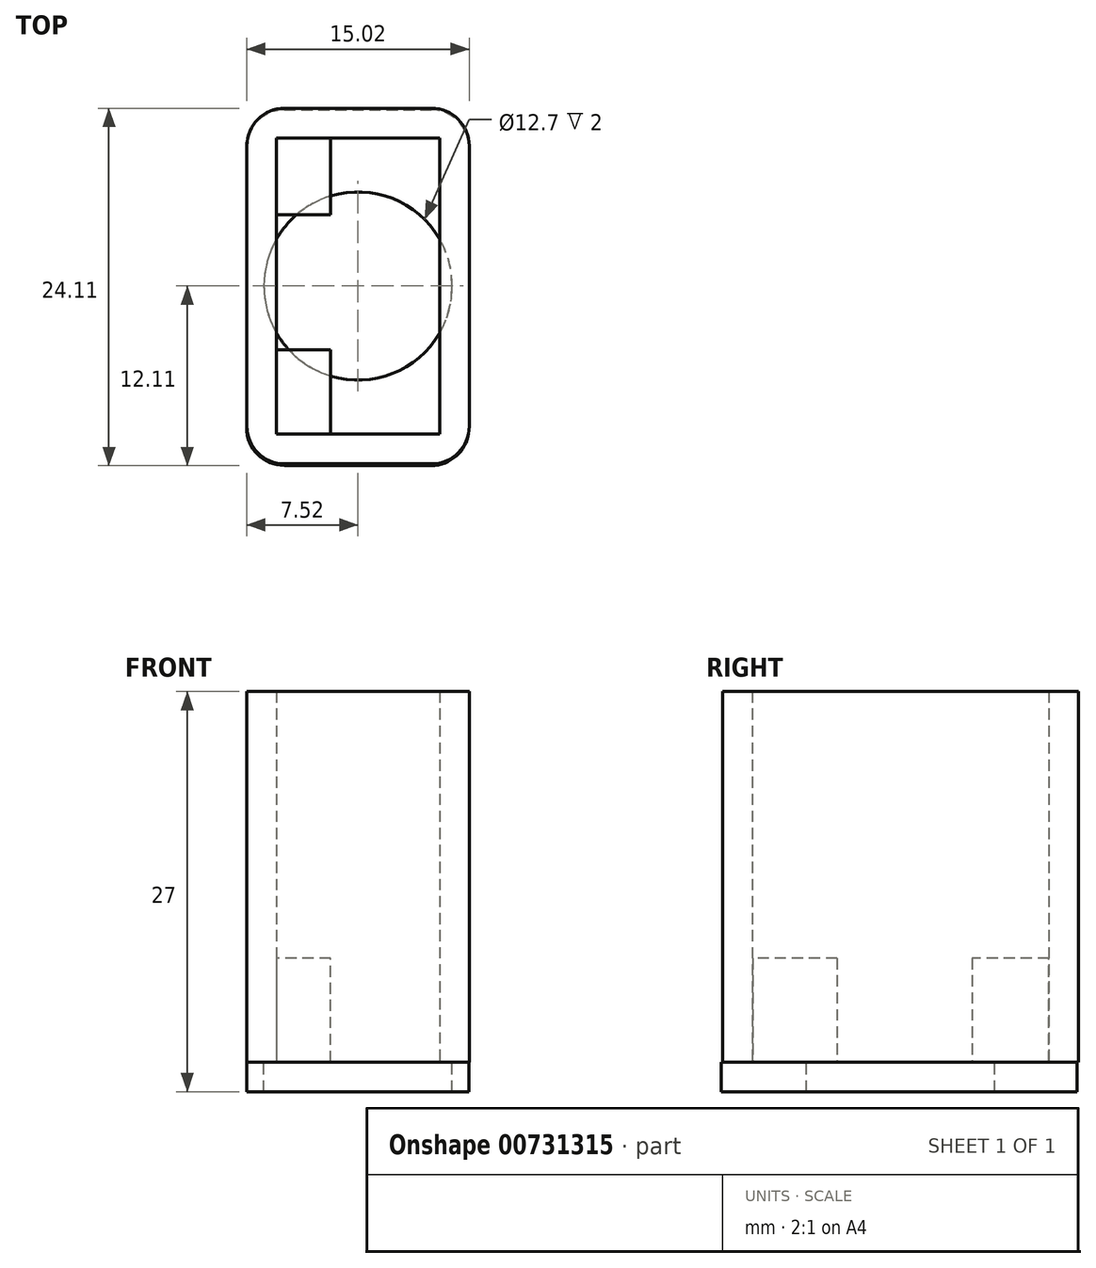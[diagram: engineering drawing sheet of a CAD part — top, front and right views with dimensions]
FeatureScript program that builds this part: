
annotation { "Feature Type Name" : "Feature", "Feature Type Description" : "" }
export const myFeature = defineFeature(function(context is Context, id is Id, definition is map)
    precondition{}
    {
        {
            var Q0;
            Q0=qCreatedBy(makeId("Top.planeOp"),FACE);
            var sketch = newSketch(context, id + "F0", { "sketchPlane" : qUnion([Q0])});
            skLineSegment(sketch, "E0.bottom", {"start": v(5.5, 10) * mm, "end": v(-5.5, 10) * mm});
            skLineSegment(sketch, "E0.top", {"start": v(5.5, -10) * mm, "end": v(-5.5, -10) * mm});
            skLineSegment(sketch, "E0.left", {"start": v(5.5, 10) * mm, "end": v(5.5, -10) * mm});
            skLineSegment(sketch, "E0.right", {"start": v(-5.5, 10) * mm, "end": v(-5.5, -10) * mm});
            skPoint(sketch, "E0.middle", {"position": v(0, 0) * mm});
            skLineSegment(sketch, "E1.bottom", {"start": v(4.96, 12) * mm, "end": v(-4.96, 12) * mm});
            skLineSegment(sketch, "E1.top", {"start": v(4.96, -12) * mm, "end": v(-4.96, -12) * mm});
            skLineSegment(sketch, "E1.left", {"start": v(7.5, 9.46) * mm, "end": v(7.5, -9.46) * mm});
            skLineSegment(sketch, "E1.right", {"start": v(-7.5, 9.46) * mm, "end": v(-7.5, -9.46) * mm});
            skPoint(sketch, "E2.visualSharp", {"position": v(-7.5, -12) * mm});
            skArc(sketch, "E2.filletArc", {"start": v(-7.5, -9.46) * mm, "mid": v(-6.76, -11.26) * mm, "end": v(-4.96, -12) * mm});
            skPoint(sketch, "E3.visualSharp", {"position": v(7.5, -12) * mm});
            skArc(sketch, "E3.filletArc", {"start": v(4.96, -12) * mm, "mid": v(6.76, -11.26) * mm, "end": v(7.5, -9.46) * mm});
            skPoint(sketch, "E4.visualSharp", {"position": v(7.5, 12) * mm});
            skArc(sketch, "E4.filletArc", {"start": v(7.5, 9.46) * mm, "mid": v(6.76, 11.26) * mm, "end": v(4.96, 12) * mm});
            skPoint(sketch, "E5.visualSharp", {"position": v(-7.5, 12) * mm});
            skArc(sketch, "E5.filletArc", {"start": v(-4.96, 12) * mm, "mid": v(-6.76, 11.26) * mm, "end": v(-7.5, 9.46) * mm});
            skSolve(sketch);
        }
        {
            var Q0;
            Q0=makeQuery(id+"F0.imprint","IMPRINT",FACE,{"disambiguationData":[TD([[makeQuery(id+"F0.imprint","IMPRINT",EDGE,{"derivedFrom":sQuery(id+"F0.wireOp",EDGE,"E0.bottom")}),-1.0]])]});
            extrude(context, id + "F1", {"entities" : qUnion([Q0]), "depth" : 25 * mm, "offsetDistance" : 25.4 * mm});
        }
        {
            var Q0;
            Q0=qCreatedBy(makeId("Top.planeOp"),FACE);
            var sketch = newSketch(context, id + "F2", { "sketchPlane" : qUnion([Q0])});
            skCircle(sketch, "E6", {"center": v(0, 0) * mm, "radius": 6.35 * mm});
            skLineSegment(sketch, "E7.bottom", {"start": v(-4.98, -12.1) * mm, "end": v(4.94, -12.1) * mm});
            skLineSegment(sketch, "E7.top", {"start": v(-4.98, 11.9) * mm, "end": v(4.94, 11.9) * mm});
            skLineSegment(sketch, "E7.left", {"start": v(-7.52, -9.57) * mm, "end": v(-7.52, 9.35) * mm});
            skLineSegment(sketch, "E7.right", {"start": v(7.48, -9.57) * mm, "end": v(7.48, 9.35) * mm});
            skPoint(sketch, "E8.visualSharp", {"position": v(-7.52, -12.1) * mm});
            skArc(sketch, "E8.filletArc", {"start": v(-7.52, -9.57) * mm, "mid": v(-6.77, -11.37) * mm, "end": v(-4.98, -12.1) * mm});
            skPoint(sketch, "E9.visualSharp", {"position": v(7.48, -12.1) * mm});
            skArc(sketch, "E9.filletArc", {"start": v(4.94, -12.1) * mm, "mid": v(6.74, -11.37) * mm, "end": v(7.48, -9.57) * mm});
            skPoint(sketch, "E10.visualSharp", {"position": v(7.48, 11.9) * mm});
            skArc(sketch, "E10.filletArc", {"start": v(7.48, 9.35) * mm, "mid": v(6.74, 11.15) * mm, "end": v(4.94, 11.9) * mm});
            skPoint(sketch, "E11.visualSharp", {"position": v(-7.52, 11.9) * mm});
            skArc(sketch, "E11.filletArc", {"start": v(-4.98, 11.9) * mm, "mid": v(-6.77, 11.15) * mm, "end": v(-7.52, 9.35) * mm});
            skSolve(sketch);
        }
        {
            var Q0;
            Q0 = qSketchRegion(id + "F2", true);
            extrude(context, id + "F3", {"entities" : qUnion([Q0]), "operationType" : NewBodyOperationType.ADD, "oppositeDirection" : true, "depth" : 2 * mm, "offsetDistance" : 25.4 * mm});
        }
        {
            var Q0;
            Q0=qCreatedBy(makeId("Top.planeOp"),FACE);
            var sketch = newSketch(context, id + "F4", { "sketchPlane" : qUnion([Q0])});
            skLineSegment(sketch, "E12.bottom", {"start": v(-5.5, 10.05) * mm, "end": v(-1.85, 10.05) * mm});
            skLineSegment(sketch, "E12.top", {"start": v(-5.5, 4.82) * mm, "end": v(-1.85, 4.82) * mm});
            skLineSegment(sketch, "E12.left", {"start": v(-5.5, 10.05) * mm, "end": v(-5.5, 4.82) * mm});
            skLineSegment(sketch, "E12.right", {"start": v(-1.85, 10.05) * mm, "end": v(-1.85, 4.82) * mm});
            skLineSegment(sketch, "E13.bottom", {"start": v(-5.5, -4.29) * mm, "end": v(-1.85, -4.29) * mm});
            skLineSegment(sketch, "E13.top", {"start": v(-5.5, -9.98) * mm, "end": v(-1.85, -9.98) * mm});
            skLineSegment(sketch, "E13.left", {"start": v(-5.5, -4.29) * mm, "end": v(-5.5, -9.98) * mm});
            skLineSegment(sketch, "E13.right", {"start": v(-1.85, -4.29) * mm, "end": v(-1.85, -9.98) * mm});
            skSolve(sketch);
        }
        {
            var Q0;
            Q0=makeQuery(id+"F4.imprint","IMPRINT",FACE,{"disambiguationData":[TD([[makeQuery(id+"F4.imprint","IMPRINT",EDGE,{"derivedFrom":sQuery(id+"F4.wireOp",EDGE,"E12.bottom")}),-1.0]])]});
            var Q1;
            Q1=makeQuery(id+"F4.imprint","IMPRINT",FACE,{"disambiguationData":[TD([[makeQuery(id+"F4.imprint","IMPRINT",EDGE,{"derivedFrom":sQuery(id+"F4.wireOp",EDGE,"E13.bottom")}),-1.0]])]});
            extrude(context, id + "F5", {"entities" : qUnion([Q0, Q1]), "operationType" : NewBodyOperationType.ADD, "depth" : 7 * mm, "offsetDistance" : 25.4 * mm});
        }
    });
